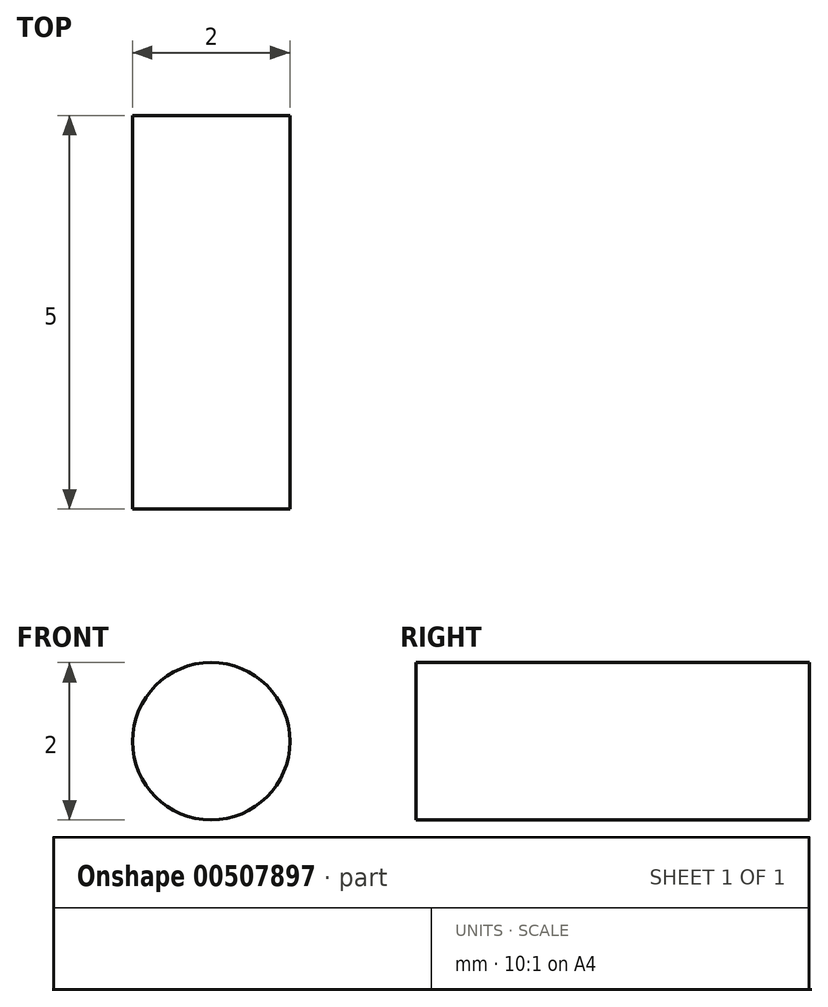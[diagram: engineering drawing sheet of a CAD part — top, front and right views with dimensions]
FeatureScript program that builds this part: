
annotation { "Feature Type Name" : "Feature", "Feature Type Description" : "" }
export const myFeature = defineFeature(function(context is Context, id is Id, definition is map)
    precondition{}
    {
        {
            var Q0;
            Q0=qCreatedBy(makeId("Front.planeOp"),FACE);
            var sketch = newSketch(context, id + "F0", { "sketchPlane" : qUnion([Q0])});
            skCircle(sketch, "E0", {"center": v(0, 0) * mm, "radius": 1 * mm});
            skSolve(sketch);
        }
        {
            var Q0;
            Q0=makeQuery(id+"F0.imprint","IMPRINT",FACE,{"disambiguationData":[TD([[makeQuery(id+"F0.imprint","IMPRINT",EDGE,{"derivedFrom":sQuery(id+"F0.wireOp",EDGE,"E0")}),1.0]])]});
            extrude(context, id + "F1", {"entities" : qUnion([Q0]), "depth" : 5 * mm, "offsetDistance" : 25 * mm});
        }
    });
